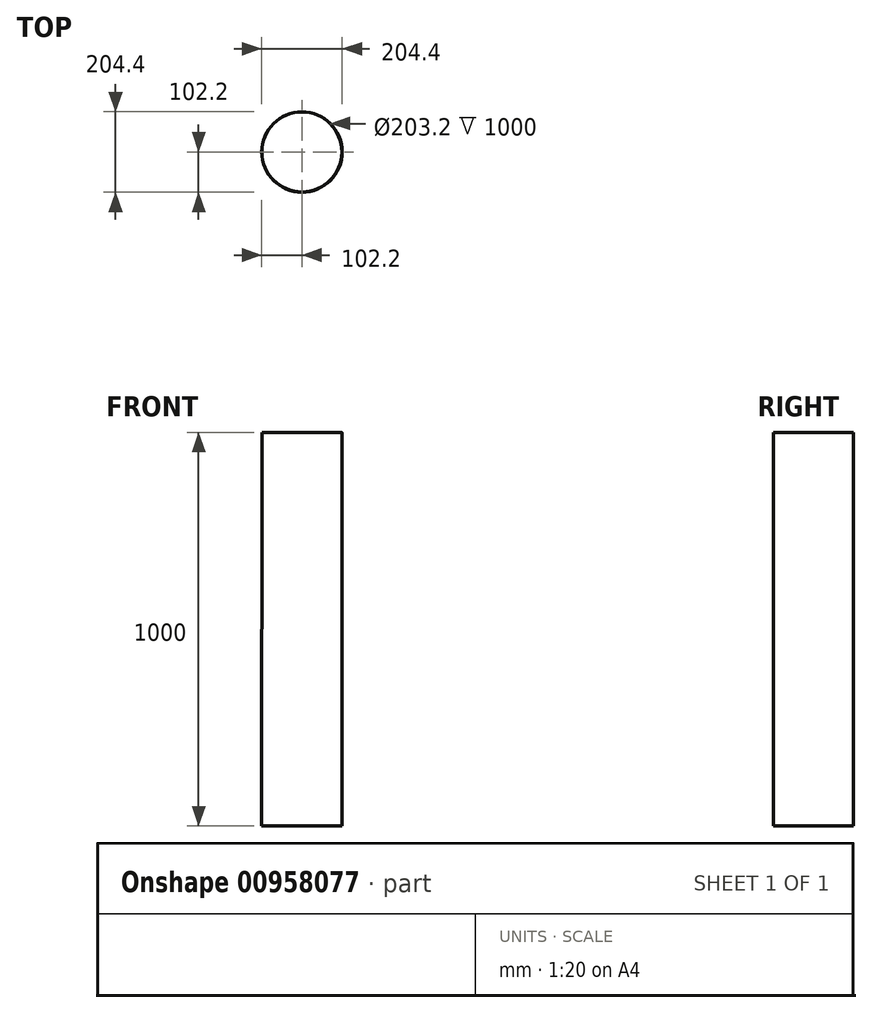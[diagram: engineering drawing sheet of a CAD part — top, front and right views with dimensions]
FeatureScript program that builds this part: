
annotation { "Feature Type Name" : "Feature", "Feature Type Description" : "" }
export const myFeature = defineFeature(function(context is Context, id is Id, definition is map)
    precondition{}
    {
        {
            var Q0;
            Q0=qCreatedBy(makeId("Front.planeOp"),FACE);
            var sketch = newSketch(context, id + "F0", { "sketchPlane" : qUnion([Q0])});
            skLineSegment(sketch, "E0", {"start": v(0, 0) * mm, "end": v(0, 1000) * mm, "construction": true});
            skSolve(sketch);
        }
        {
            var Q0;
            Q0=qCreatedBy(makeId("Front.planeOp"),FACE);
            var sketch = newSketch(context, id + "F1", { "sketchPlane" : qUnion([Q0])});
            skLineSegment(sketch, "E1", {"start": v(-101.6, 0) * mm, "end": v(-101.6, 1000) * mm});
            skLineSegment(sketch, "E2", {"start": v(-101.6, 1000) * mm, "end": v(-101.7, 1000) * mm});
            skLineSegment(sketch, "E3", {"start": v(-101.7, 1000) * mm, "end": v(-101.7, 999.81) * mm});
            skLineSegment(sketch, "E4", {"start": v(-101.7, 999.81) * mm, "end": v(-101.67, 999.79) * mm});
            skLineSegment(sketch, "E5", {"start": v(-101.67, 999.79) * mm, "end": v(-101.7, 999.77) * mm});
            skLineSegment(sketch, "E6", {"start": v(-101.7, 999.77) * mm, "end": v(-101.7, 999.76) * mm});
            skLineSegment(sketch, "E7", {"start": v(-101.7, 999.76) * mm, "end": v(-101.67, 999.75) * mm});
            skLineSegment(sketch, "E8", {"start": v(-101.67, 999.75) * mm, "end": v(-101.7, 999.75) * mm});
            skLineSegment(sketch, "E9", {"start": v(-101.6, 0) * mm, "end": v(-102.2, 0) * mm});
            skLineSegment(sketch, "E10", {"start": v(-102.2, 0) * mm, "end": v(-101.7, 999.75) * mm});
            skSolve(sketch);
        }
        {
            var Q0;
            Q0 = qConstructionFilter(qBodyType(qCreatedBy(id + "F1" ,EDGE), BodyType.WIRE), ConstructionObject.NO);
            var Q1;
            Q1=sQuery(id+"F0.wireOp",EDGE,"E0");
            revolve(context, id + "F2", {"bodyType" : ToolBodyType.SURFACE, "surfaceOperationType" : NewSurfaceOperationType.NEW, "surfaceEntities" : qUnion([Q0]), "axis" : qUnion([Q1]), "revolveType" : RevolveType.FULL});
        }
    });
